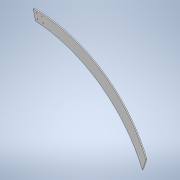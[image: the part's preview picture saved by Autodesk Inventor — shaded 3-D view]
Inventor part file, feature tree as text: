
AUTODESK INVENTOR PART (.ipt)
format: ipt  version: 2020.3 (Build 243373000, 373)  size: 173,056 bytes
history: native  units: mm
features: extrude x6, sketch x6
ambient origin geometry x8: Origin, YZ Plane, XZ Plane, XY Plane, X Axis, Y Axis, Z Axis, Center Point
bodies: Solid1 (feature_tree)
feature tree (12):
  extrude  "Extrusion1"  Depth=40.0mm
  sketch  "Sketch2"  dims[d4=3.490659mm d5=465.0mm]
  extrude  "Extrusion2"  Depth=465.0mm
  extrude  "Extrusion4"  Depth=4.0mm TaperAngle=0.0deg
  extrude  "Extrusion5"  Depth=4.0mm TaperAngle=0.0deg
  extrude  "Extrusion6"  Depth=10.0mm TaperAngle=0.0deg
  extrude  "Extrusion7"  Depth=10.0mm
  sketch  "Sketch1"  dims[d1=30.0mm d2=40.0mm]
  sketch  "Sketch4"  dims[d6=450.0mm d7=4.0mm d8=0.0mm]
  sketch  "Sketch5"  dims[d9=90.0mm d10=4.0mm d11=0.0mm]
  sketch  "Sketch6"  dims[d16=3.490659mm d17=10.0mm d18=0.0mm]
  sketch  "Sketch7"  dims[d19=10.0mm d20=0.0mm d21=10.0mm d22=700.0mm d23=6.981317mm d24=260.0mm d25=10.0mm d26=0.0mm d27=2.707006mm d28=0.698132mm d29=270.0mm d30=270.0mm d31=3.0mm d32=3.0mm d33=3.0mm d34=3.0mm d35=19.024089mm d36=20.0mm d37=0.0mm d38=0.0mm]
